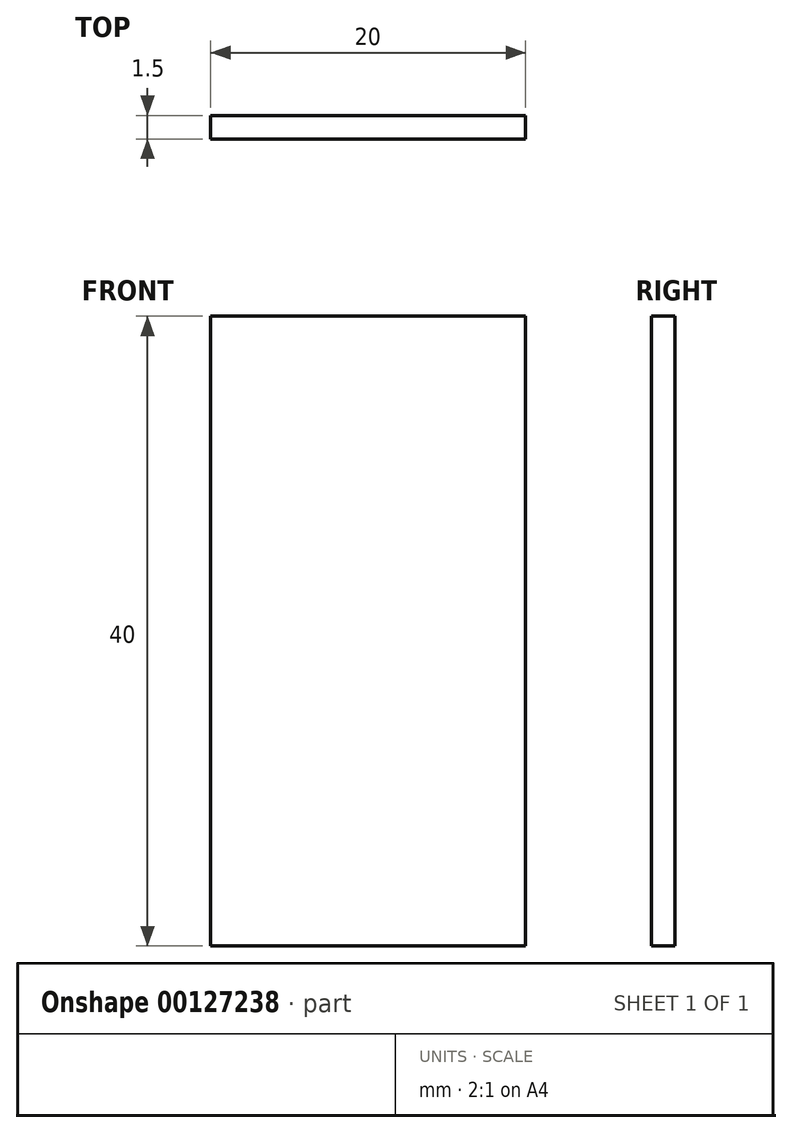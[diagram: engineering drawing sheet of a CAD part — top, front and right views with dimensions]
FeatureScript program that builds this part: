
annotation { "Feature Type Name" : "Feature", "Feature Type Description" : "" }
export const myFeature = defineFeature(function(context is Context, id is Id, definition is map)
    precondition{}
    {
        {
            var Q0;
            Q0=qCreatedBy(makeId("Front.planeOp"),FACE);
            var sketch = newSketch(context, id + "F0", { "sketchPlane" : qUnion([Q0])});
            skLineSegment(sketch, "E0.bottom", {"start": v(0, 0) * mm, "end": v(20, 0) * mm});
            skLineSegment(sketch, "E0.top", {"start": v(0, 40) * mm, "end": v(20, 40) * mm});
            skLineSegment(sketch, "E0.left", {"start": v(0, 0) * mm, "end": v(0, 40) * mm});
            skLineSegment(sketch, "E0.right", {"start": v(20, 0) * mm, "end": v(20, 40) * mm});
            skSolve(sketch);
        }
        {
            var Q0;
            Q0=makeQuery(id+"F0.imprint","IMPRINT",FACE,{"disambiguationData":[TD([[makeQuery(id+"F0.imprint","IMPRINT",EDGE,{"derivedFrom":sQuery(id+"F0.wireOp",EDGE,"E0.bottom")}),1.0]])]});
            extrude(context, id + "F1", {"entities" : qUnion([Q0]), "depth" : 1.5 * mm});
        }
    });
